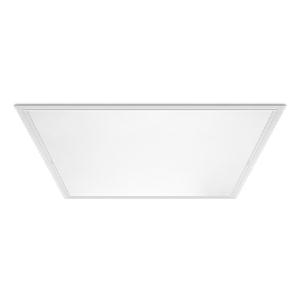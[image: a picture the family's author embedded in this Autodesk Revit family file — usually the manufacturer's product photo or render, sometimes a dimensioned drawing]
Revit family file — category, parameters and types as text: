
# Revit family: 3f_filippi_-_l_340_luce_diffusa_vs_ip65v_3f_filippi_-_23921_-_l_340_29w-940_vs_ip65v_596x596
name_source: partatom
category: Lighting Fixtures
units: mm (PartAtom-declared; Revit-internal decimal feet)

## family parameters
Cut with Voids When Loaded = No
Host = Face
Light Source = No
Part Type = Normal
Room Calculation Point = No
Round Connector Dimension = Use Diameter
Shared = No

## types (1)
- 3F Filippi - L 340 Luce Diffusa VS IP65V (1 x LED, 3155 lm, 35 W, 4000 K)
    Apparent Load = 35 VA
    Approval mark = ENEC
    CIE Flux Codes = 61 89 98 100 100
    Color Rendering = 90
    Color Temperature = 4000 K
    Control Gear = Electronic ballast
    Default Elevation = 1800 mm
    Description = ILLUMINOTECHNICAL
Luminous efficiency 100% (DLOR 100%, ULOR 0%).
Initial luminous flux of the luminaire 3155 lm.
Direct symmetric distribution.
Installation Interdistance Transv.D = 1.17 x hu - Long.D = 1.14 x hu.
Average luminance <3000 cd/m² for radial angles >65°.
Tabular UGR (CIE 117 - 4H-8H; S=0.25H; 70/50/20): RUG 17.2 - 17.
Beam angle: 91° - 88°.
Luminous efficacy 90 lm/W.
Lifetime (L93/B10): 30000 h. (tq+25°C)
Lifetime (L90/B10): 50000 h. (tq+25°C)
Lifetime (L85/B10): 80000 h. (tq+25°C)
Lifetime (L80/B10): 100000 h. (tq+25°C)
Sudden decreased luminous flux after 50000 hours: 0% (C0).
Photobiological safety in compliance with IEC/TR 62778: RG0 risk exempt, (IEC 62471).
In compliance with IEC/EN 62722-2-1 - IEC/EN 62717 standards.

SOURCE
Squared LED module 29W/940.
Energy efficiency class (UE 2019/2020 - UE 2019/2015): D.
CIE 13.3 Colour rendering index: CRI >90 (R9 >50%).
IES TM-30 Fidelity Index: Rf = 92 Rg = 101.
CCT nominal colour temperature 4000 K.
Colour initial tolerance (MacAdam): SDCM 3.

MECHANICAL
Housing in hot-galvanised steel, painted in white polyester.
Perimetral frame in white polycarbonate.
VS moulded glass, anti-glare, tempered, non-combustible, thickness 4 mm.
Luminaire with limited surface temperature. - D - (EN 60598-2-24)
Dimensions: 596x596 mm, height 80 mm. Weight 6.4 kg.
IP65 protection degree for exposed part, IP40 for recessed part.
Mechanical strength to impacts IK08 (5 joule).
Glow-wire test resistance 960°C.

ELECTRICAL
Wiring on a separate unit.
Halogen Free electronic wiring 230V-50/60Hz, power factor 0.95, THD <25%, constant output current, SELV, class II, 1 driver.
Power of the luminaire 35 W.
CE - IEC 60598-1 - EN 60598-1.
SAFE FLICKER: PstLM=<1 and SVM=<0.4 (IEC TR 61547-1 and IEC TR 63158), to ensure a more comfortable and safe light.
Luminaire compliant with EN 60598-2-22 for power supply from a centralised emergency system CPSS (Central Power Supply System), not incorporated in the luminaire - high risk areas excluded. The default power and flux are 100% in AC and 100% in DC.
Ambient temperature from 0°C to +40°C.
Temperature class T6 max 85°C.
Relative humidity UR: <85%.

INSTALLATION
Lay-on or pull-up recessed fitting using frame and anti-fall safety cable accessories.
All accessories dedicated to this product are available on the Catalog and on our website www.3F-Filippi.com.

APPLICATIONS
In environments requiring protection and simplified cleaning.
Hospitals, pharmaceutical, chemical, aseptic laboratories, sterilised rooms.
Environments: with VDTs, meeting rooms, offices.
Environments: architectural, commercial, staterooms, banks.
Environments where demanding visual tasks are performed and soft diffuse light is required for optimal visual comfort and total shielding of the light source.

WARNING
Luminaire designed for disposal/recycling at end-of-life.
Replaceable (LED only) light source by a professional. Replaceable control gear by a professional.
    Height = 0 mm  [stored 0 ft]
    Lamp = 1 x LED
    Lamp Light Flux = 3155 lm
    Lamp Power = 35 W
    Lamp count = 1
    Length = 596 mm
    Lifetime = 50000 h
    Luminous efficacy = 90 lm/W
    Manufacturer = 3F Filippi
    ModVariant = No
    Model = 3F Filippi - 23921 - L 340 29W-940 VS IP65V 596x596
    Mounting Place = Ceiling
    Mounting Type = Recessed
    Number of Poles = 1
    OnlyDefault = Yes
    Power Factor = 1
    Product Name = 3F Filippi - L 340 Luce Diffusa VS IP65V
    Product group = recessed luminaire
    ProductGroupID = 4
    Protection Class = Protection class II
    Protection Degree = IP 40
    RLX_Detail_Level = 1
    RLX_Emergency_Light_Flux = 0 lm
    RLX_Emergency_Type = 0
    RLX_Emergency_Type_DB = No
    RlxData = <blob elided: 152653 chars, md5=9d2d5042>
    Socket = socket
    Standby Power = 0 W
    System Light Flux = 3155 lm
    System Power = 35 W
    Type Comments = Product without accessories
    Type Image = 3ffilippi_l_340_luce_diffusa_vs.jpg
    URL = http://relux.com
    VarID = ---
    Voltage = 0 V
    Weight = 0.00 kg
    Width = 596 mm

note: [stored X ft] marks values corroborated as IEEE doubles in the binary element streams (Revit-internal decimal feet)

## geometry (parser evidence)
native form markers: Blend x4, Sweep x12
no freeform markers — native parametric forms only
